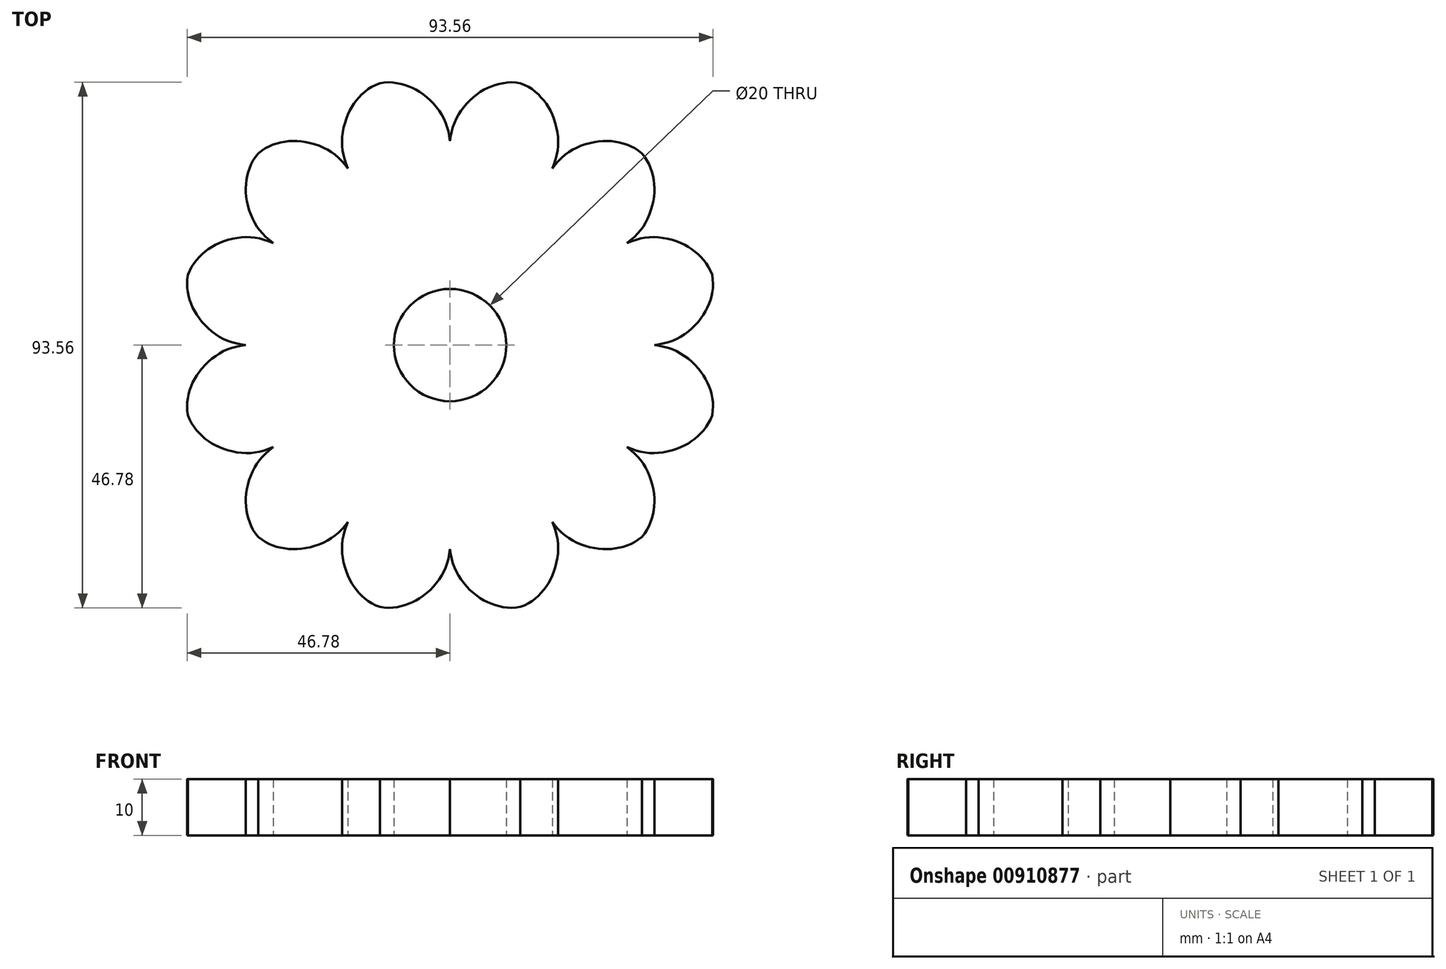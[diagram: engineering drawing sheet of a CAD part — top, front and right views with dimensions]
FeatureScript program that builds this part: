
annotation { "Feature Type Name" : "Feature", "Feature Type Description" : "" }
export const myFeature = defineFeature(function(context is Context, id is Id, definition is map)
    precondition{}
    {
        {
            var Q0;
            Q0=qCreatedBy(makeId("Top.planeOp"),FACE);
            var sketch = newSketch(context, id + "F0", { "sketchPlane" : qUnion([Q0])});
            skLineSegment(sketch, "E0", {"start": v(0, 0) * mm, "end": v(-49.17, 0) * mm, "construction": true});
            skCircle(sketch, "E1", {"center": v(0, 0) * mm, "radius": 10 * mm});
            skFitSpline(sketch, "E2", {"points": [v(-31.47, 18.17) * mm, v(-34.8, 21.83) * mm, v(-36.27, 26.5) * mm, v(-36, 30.41) * mm, v(-34.12, 34.12) * mm], "startDerivative": vector(-16.66, 12.43) * mm, "endDerivative": vector(12.57, 13.92) * mm});
            skFitSpline(sketch, "E3.MirrorCS", {"points": [v(-18.17, 31.47) * mm, v(-21.83, 34.8) * mm, v(-26.5, 36.27) * mm, v(-30.41, 36) * mm, v(-34.12, 34.12) * mm], "startDerivative": vector(-12.43, 16.66) * mm, "endDerivative": vector(-13.92, -12.57) * mm});
            skFitSpline(sketch, "E4.MirrorCS", {"points": [v(-36.34, 0) * mm, v(-41.06, 1.5) * mm, v(-44.67, 4.82) * mm, v(-46.4, 8.34) * mm, v(-46.62, 12.5) * mm], "startDerivative": vector(-20.64, 2.43) * mm, "endDerivative": vector(3.93, 18.34) * mm});
            skFitSpline(sketch, "E5.MirrorCS", {"points": [v(-31.47, 18.17) * mm, v(-36.31, 19.22) * mm, v(-41.1, 18.16) * mm, v(-44.34, 15.98) * mm, v(-46.62, 12.5) * mm], "startDerivative": vector(-19.1, 8.22) * mm, "endDerivative": vector(-5.77, -17.84) * mm});
            skLineSegment(sketch, "E6.MirrorCS", {"start": v(0, 0) * mm, "end": v(-36.34, 0) * mm});
            skFitSpline(sketch, "E7.MirrorCS", {"points": [v(-18.17, 31.47) * mm, v(-19.22, 36.31) * mm, v(-18.16, 41.1) * mm, v(-15.98, 44.34) * mm, v(-12.5, 46.62) * mm], "startDerivative": vector(-8.22, 19.1) * mm, "endDerivative": vector(17.84, 5.77) * mm});
            skFitSpline(sketch, "E8.MirrorCS", {"points": [v(0, 36.34) * mm, v(-1.5, 41.06) * mm, v(-4.82, 44.67) * mm, v(-8.34, 46.4) * mm, v(-12.5, 46.62) * mm], "startDerivative": vector(-2.43, 20.64) * mm, "endDerivative": vector(-18.34, -3.93) * mm});
            skLineSegment(sketch, "E9.MirrorCS", {"start": v(0, 0) * mm, "end": v(36.34, 0) * mm});
            skFitSpline(sketch, "E10.MirrorCS", {"points": [v(0, 36.34) * mm, v(1.5, 41.06) * mm, v(4.82, 44.67) * mm, v(8.34, 46.4) * mm, v(12.5, 46.62) * mm], "startDerivative": vector(2.43, 20.64) * mm, "endDerivative": vector(18.34, -3.93) * mm});
            skFitSpline(sketch, "E11.MirrorCS", {"points": [v(31.47, 18.17) * mm, v(34.8, 21.83) * mm, v(36.27, 26.5) * mm, v(36, 30.41) * mm, v(34.12, 34.12) * mm], "startDerivative": vector(16.66, 12.43) * mm, "endDerivative": vector(-12.57, 13.92) * mm});
            skFitSpline(sketch, "E12.MirrorCS", {"points": [v(31.47, 18.17) * mm, v(36.31, 19.22) * mm, v(41.1, 18.16) * mm, v(44.34, 15.98) * mm, v(46.62, 12.5) * mm], "startDerivative": vector(19.1, 8.22) * mm, "endDerivative": vector(5.77, -17.84) * mm});
            skLineSegment(sketch, "E13.MirrorCS", {"start": v(0, 0) * mm, "end": v(49.17, 0) * mm, "construction": true});
            skFitSpline(sketch, "E14.MirrorCS", {"points": [v(36.34, 0) * mm, v(41.06, 1.5) * mm, v(44.67, 4.82) * mm, v(46.4, 8.34) * mm, v(46.62, 12.5) * mm], "startDerivative": vector(20.64, 2.43) * mm, "endDerivative": vector(-3.93, 18.34) * mm});
            skFitSpline(sketch, "E15.MirrorCS", {"points": [v(18.17, 31.47) * mm, v(19.22, 36.31) * mm, v(18.16, 41.1) * mm, v(15.98, 44.34) * mm, v(12.5, 46.62) * mm], "startDerivative": vector(8.22, 19.1) * mm, "endDerivative": vector(-17.84, 5.77) * mm});
            skFitSpline(sketch, "E16.MirrorCS", {"points": [v(18.17, 31.47) * mm, v(21.83, 34.8) * mm, v(26.5, 36.27) * mm, v(30.41, 36) * mm, v(34.12, 34.12) * mm], "startDerivative": vector(12.43, 16.66) * mm, "endDerivative": vector(13.92, -12.57) * mm});
            skFitSpline(sketch, "E17.MirrorCS", {"points": [v(-31.47, -18.17) * mm, v(-36.31, -19.22) * mm, v(-41.1, -18.16) * mm, v(-44.34, -15.98) * mm, v(-46.62, -12.5) * mm], "startDerivative": vector(-19.1, -8.22) * mm, "endDerivative": vector(-5.77, 17.84) * mm});
            skFitSpline(sketch, "E18.MirrorCS", {"points": [v(0, -36.34) * mm, v(-1.5, -41.06) * mm, v(-4.82, -44.67) * mm, v(-8.34, -46.4) * mm, v(-12.5, -46.62) * mm], "startDerivative": vector(-2.43, -20.64) * mm, "endDerivative": vector(-18.34, 3.93) * mm});
            skFitSpline(sketch, "E19.MirrorCS", {"points": [v(18.17, -31.47) * mm, v(19.22, -36.31) * mm, v(18.16, -41.1) * mm, v(15.98, -44.34) * mm, v(12.5, -46.62) * mm], "startDerivative": vector(8.22, -19.1) * mm, "endDerivative": vector(-17.84, -5.77) * mm});
            skFitSpline(sketch, "E20.MirrorCS", {"points": [v(-18.17, -31.47) * mm, v(-19.22, -36.31) * mm, v(-18.16, -41.1) * mm, v(-15.98, -44.34) * mm, v(-12.5, -46.62) * mm], "startDerivative": vector(-8.22, -19.1) * mm, "endDerivative": vector(17.84, -5.77) * mm});
            skFitSpline(sketch, "E21.MirrorCS", {"points": [v(0, -36.34) * mm, v(1.5, -41.06) * mm, v(4.82, -44.67) * mm, v(8.34, -46.4) * mm, v(12.5, -46.62) * mm], "startDerivative": vector(2.43, -20.64) * mm, "endDerivative": vector(18.34, 3.93) * mm});
            skFitSpline(sketch, "E22.MirrorCS", {"points": [v(-18.17, -31.47) * mm, v(-21.83, -34.8) * mm, v(-26.5, -36.27) * mm, v(-30.41, -36) * mm, v(-34.12, -34.12) * mm], "startDerivative": vector(-12.43, -16.66) * mm, "endDerivative": vector(-13.92, 12.57) * mm});
            skFitSpline(sketch, "E23.MirrorCS", {"points": [v(31.47, -18.17) * mm, v(34.8, -21.83) * mm, v(36.27, -26.5) * mm, v(36, -30.41) * mm, v(34.12, -34.12) * mm], "startDerivative": vector(16.66, -12.43) * mm, "endDerivative": vector(-12.57, -13.92) * mm});
            skFitSpline(sketch, "E24.MirrorCS", {"points": [v(18.17, -31.47) * mm, v(21.83, -34.8) * mm, v(26.5, -36.27) * mm, v(30.41, -36) * mm, v(34.12, -34.12) * mm], "startDerivative": vector(12.43, -16.66) * mm, "endDerivative": vector(13.92, 12.57) * mm});
            skFitSpline(sketch, "E25.MirrorCS", {"points": [v(-31.47, -18.17) * mm, v(-34.8, -21.83) * mm, v(-36.27, -26.5) * mm, v(-36, -30.41) * mm, v(-34.12, -34.12) * mm], "startDerivative": vector(-16.66, -12.43) * mm, "endDerivative": vector(12.57, -13.92) * mm});
            skFitSpline(sketch, "E26.MirrorCS", {"points": [v(31.47, -18.17) * mm, v(36.31, -19.22) * mm, v(41.1, -18.16) * mm, v(44.34, -15.98) * mm, v(46.62, -12.5) * mm], "startDerivative": vector(19.1, -8.22) * mm, "endDerivative": vector(5.77, 17.84) * mm});
            skFitSpline(sketch, "E27.MirrorCS", {"points": [v(36.34, 0) * mm, v(41.06, -1.5) * mm, v(44.67, -4.82) * mm, v(46.4, -8.34) * mm, v(46.62, -12.5) * mm], "startDerivative": vector(20.64, -2.43) * mm, "endDerivative": vector(-3.93, -18.34) * mm});
            skFitSpline(sketch, "E28.MirrorCS", {"points": [v(-36.34, 0) * mm, v(-41.06, -1.5) * mm, v(-44.67, -4.82) * mm, v(-46.4, -8.34) * mm, v(-46.62, -12.5) * mm], "startDerivative": vector(-20.64, -2.43) * mm, "endDerivative": vector(3.93, -18.34) * mm});
            skSolve(sketch);
        }
        {
            var Q0;
            Q0=makeQuery(id+"F0.imprint","IMPRINT",FACE,{"disambiguationData":[TD([[makeQuery(id+"F0.imprint","IMPRINT",EDGE,{"derivedFrom":sQuery(id+"F0.wireOp",EDGE,"E2")}),-1.0]])]});
            var Q1;
            Q1=makeQuery(id+"F0.imprint","IMPRINT",FACE,{"disambiguationData":[TD([[makeQuery(id+"F0.imprint","IMPRINT",EDGE,{"derivedFrom":sQuery(id+"F0.wireOp",EDGE,"E17.MirrorCS")}),-1.0]])]});
            extrude(context, id + "F1", {"entities" : qUnion([Q0, Q1]), "depth" : 10 * mm, "offsetDistance" : 25.4 * mm});
        }
    });
